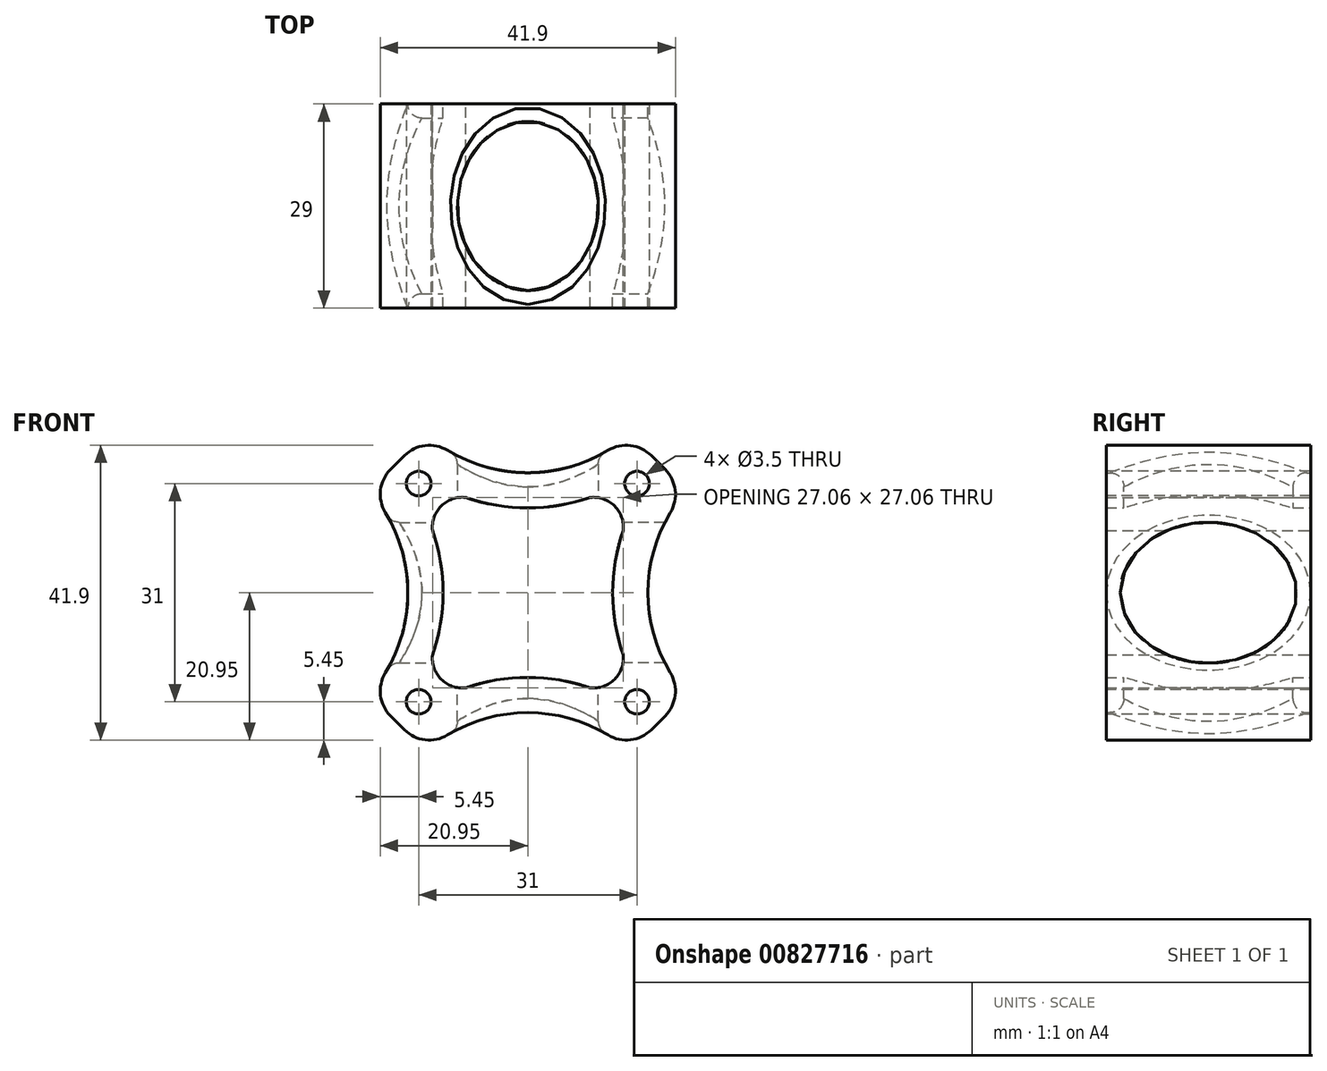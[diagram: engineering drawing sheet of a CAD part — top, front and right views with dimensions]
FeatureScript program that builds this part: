
annotation { "Feature Type Name" : "Feature", "Feature Type Description" : "" }
export const myFeature = defineFeature(function(context is Context, id is Id, definition is map)
    precondition{}
    {
        {
            var Q0;
            Q0=qCreatedBy(makeId("Front.planeOp"),FACE);
            var sketch = newSketch(context, id + "F0", { "sketchPlane" : qUnion([Q0])});
            skLineSegment(sketch, "E0.bottom", {"start": v(-15.5, 15.5) * mm, "end": v(15.5, 15.5) * mm, "construction": true});
            skLineSegment(sketch, "E0.top", {"start": v(-15.5, -15.5) * mm, "end": v(15.5, -15.5) * mm, "construction": true});
            skLineSegment(sketch, "E0.left", {"start": v(-15.5, 15.5) * mm, "end": v(-15.5, -15.5) * mm, "construction": true});
            skLineSegment(sketch, "E0.right", {"start": v(15.5, 15.5) * mm, "end": v(15.5, -15.5) * mm, "construction": true});
            skPoint(sketch, "E0.middle", {"position": v(0, 0) * mm});
            skCircle(sketch, "E1", {"center": v(-15.5, 15.5) * mm, "radius": 2.75 * mm, "construction": true});
            skCircle(sketch, "E2", {"center": v(15.5, 15.5) * mm, "radius": 2.75 * mm, "construction": true});
            skCircle(sketch, "E3", {"center": v(-15.5, -15.5) * mm, "radius": 2.75 * mm, "construction": true});
            skCircle(sketch, "E4", {"center": v(15.5, -15.5) * mm, "radius": 2.75 * mm, "construction": true});
            skCircle(sketch, "E5", {"center": v(0, 0) * mm, "radius": 6.6 * mm});
            skLineSegment(sketch, "E6.bottom", {"start": v(14.5, 22.5) * mm, "end": v(-14.5, 22.5) * mm});
            skLineSegment(sketch, "E6.top", {"start": v(14.5, -22.5) * mm, "end": v(-14.5, -22.5) * mm});
            skLineSegment(sketch, "E6.left", {"start": v(22.5, 14.5) * mm, "end": v(22.5, 0) * mm});
            skLineSegment(sketch, "E6.right", {"start": v(-22.5, 14.5) * mm, "end": v(-22.5, 0) * mm});
            skPoint(sketch, "E7.visualSharp", {"position": v(-22.5, 22.5) * mm});
            skPoint(sketch, "E8.visualSharp", {"position": v(22.5, 22.5) * mm});
            skPoint(sketch, "E9.visualSharp", {"position": v(22.5, -22.5) * mm});
            skPoint(sketch, "E10.visualSharp", {"position": v(-22.5, -22.5) * mm});
            skLineSegment(sketch, "E11", {"start": v(-22.5, 0) * mm, "end": v(-22.5, -14.5) * mm});
            skLineSegment(sketch, "E12", {"start": v(22.5, 0) * mm, "end": v(22.5, -14.5) * mm});
            skArc(sketch, "E13", {"start": v(-22.5, -14.5) * mm, "mid": v(-17.05, 0) * mm, "end": v(-22.5, 14.5) * mm});
            skArc(sketch, "E14", {"start": v(-14.5, 22.5) * mm, "mid": v(0, 17.05) * mm, "end": v(14.5, 22.5) * mm});
            skArc(sketch, "E15", {"start": v(22.5, 14.5) * mm, "mid": v(17.05, 0) * mm, "end": v(22.5, -14.5) * mm});
            skArc(sketch, "E16", {"start": v(14.5, -22.5) * mm, "mid": v(0, -17.05) * mm, "end": v(-14.5, -22.5) * mm});
            skArc(sketch, "E17", {"start": v(-8.83, 13.53) * mm, "mid": v(0, 12.05) * mm, "end": v(8.83, 13.53) * mm});
            skArc(sketch, "E18", {"start": v(-8.83, 13.53) * mm, "mid": v(-12.3, 12.3) * mm, "end": v(-13.53, 8.83) * mm});
            skArc(sketch, "E19.1.0", {"start": v(-13.53, -8.83) * mm, "mid": v(-12.3, -12.3) * mm, "end": v(-8.83, -13.53) * mm});
            skArc(sketch, "E19.2.0", {"start": v(8.83, -13.53) * mm, "mid": v(12.3, -12.3) * mm, "end": v(13.53, -8.83) * mm});
            skArc(sketch, "E19.3.0", {"start": v(13.53, 8.83) * mm, "mid": v(12.3, 12.3) * mm, "end": v(8.83, 13.53) * mm});
            skArc(sketch, "E20", {"start": v(13.53, 8.83) * mm, "mid": v(12.05, 0) * mm, "end": v(13.53, -8.83) * mm});
            skArc(sketch, "E21", {"start": v(8.83, -13.53) * mm, "mid": v(0, -12.05) * mm, "end": v(-8.83, -13.53) * mm});
            skArc(sketch, "E22", {"start": v(-13.53, -8.83) * mm, "mid": v(-12.05, 0) * mm, "end": v(-13.53, 8.83) * mm});
            skLineSegment(sketch, "E23", {"start": v(-22.5, 14.5) * mm, "end": v(-14.5, 22.5) * mm});
            skLineSegment(sketch, "E24", {"start": v(14.5, 22.5) * mm, "end": v(22.5, 14.5) * mm});
            skLineSegment(sketch, "E25", {"start": v(22.5, -14.5) * mm, "end": v(14.5, -22.5) * mm});
            skLineSegment(sketch, "E26", {"start": v(-14.5, -22.5) * mm, "end": v(-22.5, -14.5) * mm});
            skSolve(sketch);
        }
        {
            var Q0;
            Q0=makeQuery(id+"F0.imprint","IMPRINT",FACE,{"disambiguationData":[TD([[makeQuery(id+"F0.imprint","IMPRINT",EDGE,{"derivedFrom":sQuery(id+"F0.wireOp",EDGE,"E13")}),-1.0]])]});
            extrude(context, id + "F1", {"entities" : qUnion([Q0]), "flatOperationType" : FlatOperationType.REMOVE, "depth" : 29 * mm, "offsetDistance" : 25 * mm, "domain" : OperationDomain.MODEL});
        }
        {
            var Q0;
            Q0=sQuery(id+"F0.wireOp",VERTEX,"E0.bottom.end");
            var Q1;
            Q1=sQuery(id+"F0.wireOp",VERTEX,"E0.bottom.start");
            var Q2;
            Q2=sQuery(id+"F0.wireOp",VERTEX,"E0.top.start");
            var Q3;
            Q3=sQuery(id+"F0.wireOp",VERTEX,"E0.top.end");
            var Q4;
            Q4=makeQuery(id+"F1.opExtrude","SWEPT_BODY",BODY,{"disambiguationData":[OSD([sQuery(id+"F0.wireOp",EDGE,"E7.filletArc"),sQuery(id+"F0.wireOp",EDGE,"E8.filletArc"),sQuery(id+"F0.wireOp",EDGE,"E9.filletArc"),sQuery(id+"F0.wireOp",EDGE,"E10.filletArc"),sQuery(id+"F0.wireOp",EDGE,"E13"),sQuery(id+"F0.wireOp",EDGE,"E14"),sQuery(id+"F0.wireOp",EDGE,"E15"),sQuery(id+"F0.wireOp",EDGE,"E16"),sQuery(id+"F0.wireOp",EDGE,"E17"),sQuery(id+"F0.wireOp",EDGE,"E18"),sQuery(id+"F0.wireOp",EDGE,"E19.1.0"),sQuery(id+"F0.wireOp",EDGE,"E19.2.0"),sQuery(id+"F0.wireOp",EDGE,"E19.3.0"),sQuery(id+"F0.wireOp",EDGE,"E20"),sQuery(id+"F0.wireOp",EDGE,"E21"),sQuery(id+"F0.wireOp",EDGE,"E22")])]});
            hole(context, id + "F2", {"style" : HoleStyle.SIMPLE, "endStyle" : HoleEndStyle.THROUGH, "oppositeDirection" : true, "holeDiameter" : 3.5 * mm, "majorDiameter" : 5 * mm, "isTappedThrough" : true, "tappedDepth" : 12 * mm, "tapClearance" : 3, "locations" : qUnion([Q0, Q1, Q2, Q3]), "scope" : qUnion([Q4]), "startStyle" : HoleStartStyle.PART});
        }
        {
            var Q0;
            Q0=makeQuery(id+"F1.opExtrude","SWEPT_EDGE",EDGE,{"disambiguationData":[OSD([sQuery(id+"F0.wireOp",EDGE,"E6.right"),sQuery(id+"F0.wireOp",EDGE,"E13"),sQuery(id+"F0.wireOp",EDGE,"E23")])]});
            var Q1;
            Q1=makeQuery(id+"F1.opExtrude","SWEPT_EDGE",EDGE,{"disambiguationData":[OSD([sQuery(id+"F0.wireOp",EDGE,"E6.bottom"),sQuery(id+"F0.wireOp",EDGE,"E14"),sQuery(id+"F0.wireOp",EDGE,"E23")])]});
            var Q2;
            Q2=makeQuery(id+"F1.opExtrude","SWEPT_EDGE",EDGE,{"disambiguationData":[OSD([sQuery(id+"F0.wireOp",EDGE,"E6.bottom"),sQuery(id+"F0.wireOp",EDGE,"E14"),sQuery(id+"F0.wireOp",EDGE,"E24")])]});
            var Q3;
            Q3=makeQuery(id+"F1.opExtrude","SWEPT_EDGE",EDGE,{"disambiguationData":[OSD([sQuery(id+"F0.wireOp",EDGE,"E6.left"),sQuery(id+"F0.wireOp",EDGE,"E15"),sQuery(id+"F0.wireOp",EDGE,"E24")])]});
            var Q4;
            Q4=makeQuery(id+"F1.opExtrude","SWEPT_EDGE",EDGE,{"disambiguationData":[OSD([sQuery(id+"F0.wireOp",EDGE,"E12"),sQuery(id+"F0.wireOp",EDGE,"E15"),sQuery(id+"F0.wireOp",EDGE,"E25")])]});
            var Q5;
            Q5=makeQuery(id+"F1.opExtrude","SWEPT_EDGE",EDGE,{"disambiguationData":[OSD([sQuery(id+"F0.wireOp",EDGE,"E6.top"),sQuery(id+"F0.wireOp",EDGE,"E16"),sQuery(id+"F0.wireOp",EDGE,"E25")])]});
            var Q6;
            Q6=makeQuery(id+"F1.opExtrude","SWEPT_EDGE",EDGE,{"disambiguationData":[OSD([sQuery(id+"F0.wireOp",EDGE,"E6.top"),sQuery(id+"F0.wireOp",EDGE,"E16"),sQuery(id+"F0.wireOp",EDGE,"E26")])]});
            var Q7;
            Q7=makeQuery(id+"F1.opExtrude","SWEPT_EDGE",EDGE,{"disambiguationData":[OSD([sQuery(id+"F0.wireOp",EDGE,"E11"),sQuery(id+"F0.wireOp",EDGE,"E13"),sQuery(id+"F0.wireOp",EDGE,"E26")])]});
            fillet(context, id + "F3", {"entities" : qUnion([Q0, Q1, Q2, Q3, Q4, Q5, Q6, Q7]), "radius" : 5 * mm, "tangentPropagation" : true, "allowEdgeOverflow" : false});
        }
        {
            var Q0;
            Q0=qCreatedBy(makeId("Right.planeOp"),FACE);
            cPlane(context, id + "F4", {"entities" : qUnion([Q0]), "cplaneType" : CPlaneType.OFFSET, "offset" : 25 * mm, "width" : 150 * mm, "height" : 150 * mm});
        }
        {
            var Q0;
            Q0=qCreatedBy(id+"F4.planeOp",FACE);
            var sketch = newSketch(context, id + "F5", { "sketchPlane" : qUnion([Q0])});
            skArc(sketch, "E27", {"start": v(-2.5, 0) * mm, "mid": v(-14.5, 12) * mm, "end": v(-26.5, 0) * mm, "construction": true});
            skLineSegment(sketch, "E28", {"start": v(0, 0) * mm, "end": v(-29, 0) * mm});
            skCircle(sketch, "E29", {"center": v(-14.5, 0) * mm, "radius": 12 * mm, "construction": true});
            skEllipse(sketch, "E30", {"center": v(-14.5, 0) * mm, "majorRadius": 10 * mm, "minorRadius": 12.5 * mm, "majorAxis": v(0, 1)});
            skSolve(sketch);
        }
        {
            var Q0;
            Q0 = qSketchRegion(id + "F5", true);
            extrude(context, id + "F6", {"entities" : qUnion([Q0]), "operationType" : NewBodyOperationType.REMOVE, "oppositeDirection" : true, "depth" : 60 * mm, "offsetDistance" : 25 * mm});
        }
        {
            var Q0;
            Q0=qCreatedBy(makeId("Top.planeOp"),FACE);
            cPlane(context, id + "F7", {"entities" : qUnion([Q0]), "cplaneType" : CPlaneType.OFFSET, "offset" : 25 * mm, "width" : 150 * mm, "height" : 150 * mm});
        }
        {
            var Q0;
            Q0=qCreatedBy(id+"F7.planeOp",FACE);
            var sketch = newSketch(context, id + "F8", { "sketchPlane" : qUnion([Q0])});
            skLineSegment(sketch, "E31", {"start": v(0, 0) * mm, "end": v(0, -29) * mm});
            skCircle(sketch, "E32", {"center": v(0, -14.5) * mm, "radius": 12 * mm, "construction": true});
            skEllipse(sketch, "E33", {"center": v(0, -14.5) * mm, "majorRadius": 10 * mm, "minorRadius": 12 * mm, "majorAxis": v(-1, 0)});
            skSolve(sketch);
        }
        {
            var Q0;
            {var subQ0=sQuery(id+"F8.wireOp",EDGE,"E32");var subQ1=sQuery(id+"F8.wireOp",EDGE,"E31");var subQ2=makeQuery(id+"F8.imprint","INTERSECT",VERTEX,{"disambiguationData":[OD(0.0)],"derivedFrom":[subQ1,subQ0]});Q0=makeQuery(id+"F8.imprint","IMPRINT",FACE,{"disambiguationData":[TD([[makeQuery(id+"F8.imprint","IMPRINT",EDGE,{"disambiguationData":[TD([[subQ2,1.0]])],"derivedFrom":subQ1}),1.0]])]});}
            var Q1;
            {var subQ0=sQuery(id+"F8.wireOp",EDGE,"E32");var subQ1=sQuery(id+"F8.wireOp",EDGE,"E31");var subQ2=makeQuery(id+"F8.imprint","INTERSECT",VERTEX,{"disambiguationData":[OD(0.0)],"derivedFrom":[subQ1,subQ0]});Q1=makeQuery(id+"F8.imprint","IMPRINT",FACE,{"disambiguationData":[TD([[makeQuery(id+"F8.imprint","IMPRINT",EDGE,{"disambiguationData":[TD([[subQ2,1.0]])],"derivedFrom":subQ1}),-1.0]])]});}
            extrude(context, id + "F9", {"entities" : qUnion([Q0, Q1]), "operationType" : NewBodyOperationType.REMOVE, "oppositeDirection" : true, "depth" : 60 * mm, "offsetDistance" : 25 * mm});
        }
        {
            var Q0;
            Q0=makeQuery(id+"F9.boolean.opBoolean","INTERSECT",EDGE,{"disambiguationData":[OD(0.0)],"derivedFrom":[makeQuery(id+"F1.opExtrude","SWEPT_FACE",FACE,{"disambiguationData":[OSD([sQuery(id+"F0.wireOp",EDGE,"E14")])]}),makeQuery(id+"F9.opExtrude","SWEPT_FACE",FACE,{"disambiguationData":[OSD([sQuery(id+"F8.wireOp",EDGE,"E33")])]})]});
            var Q1;
            Q1=makeQuery(id+"F9.boolean.opBoolean","INTERSECT",EDGE,{"derivedFrom":[makeQuery(id+"F3.opFillet","BLEND_FACE",FACE,{"disambiguationData":[OSD([sQuery(id+"F0.wireOp",EDGE,"E6.bottom"),sQuery(id+"F0.wireOp",EDGE,"E14"),sQuery(id+"F0.wireOp",EDGE,"E23")])]}),makeQuery(id+"F9.opExtrude","SWEPT_FACE",FACE,{"disambiguationData":[OSD([sQuery(id+"F8.wireOp",EDGE,"E33")])]})]});
            var Q2;
            Q2=makeQuery(id+"F9.boolean.opBoolean","INTERSECT",EDGE,{"disambiguationData":[OD(1.0)],"derivedFrom":[makeQuery(id+"F1.opExtrude","SWEPT_FACE",FACE,{"disambiguationData":[OSD([sQuery(id+"F0.wireOp",EDGE,"E14")])]}),makeQuery(id+"F9.opExtrude","SWEPT_FACE",FACE,{"disambiguationData":[OSD([sQuery(id+"F8.wireOp",EDGE,"E33")])]})]});
            var Q3;
            Q3=makeQuery(id+"F9.boolean.opBoolean","INTERSECT",EDGE,{"derivedFrom":[makeQuery(id+"F3.opFillet","BLEND_FACE",FACE,{"disambiguationData":[OSD([sQuery(id+"F0.wireOp",EDGE,"E6.bottom"),sQuery(id+"F0.wireOp",EDGE,"E14"),sQuery(id+"F0.wireOp",EDGE,"E24")])]}),makeQuery(id+"F9.opExtrude","SWEPT_FACE",FACE,{"disambiguationData":[OSD([sQuery(id+"F8.wireOp",EDGE,"E33")])]})]});
            var Q4;
            Q4=makeQuery(id+"F6.boolean.opBoolean","INTERSECT",EDGE,{"disambiguationData":[OD(0.0)],"derivedFrom":[makeQuery(id+"F1.opExtrude","SWEPT_FACE",FACE,{"disambiguationData":[OSD([sQuery(id+"F0.wireOp",EDGE,"E13")])]}),makeQuery(id+"F6.opExtrude","SWEPT_FACE",FACE,{"disambiguationData":[OSD([sQuery(id+"F5.wireOp",EDGE,"E30")])]})]});
            var Q5;
            Q5=makeQuery(id+"F6.boolean.opBoolean","INTERSECT",EDGE,{"derivedFrom":[makeQuery(id+"F3.opFillet","BLEND_FACE",FACE,{"disambiguationData":[OSD([sQuery(id+"F0.wireOp",EDGE,"E6.left"),sQuery(id+"F0.wireOp",EDGE,"E15"),sQuery(id+"F0.wireOp",EDGE,"E24")])]}),makeQuery(id+"F6.opExtrude","SWEPT_FACE",FACE,{"disambiguationData":[OSD([sQuery(id+"F5.wireOp",EDGE,"E30")])]})]});
            var Q6;
            Q6=makeQuery(id+"F9.boolean.opBoolean","INTERSECT",EDGE,{"disambiguationData":[OD(0.0)],"derivedFrom":[makeQuery(id+"F1.opExtrude","SWEPT_FACE",FACE,{"disambiguationData":[OSD([sQuery(id+"F0.wireOp",EDGE,"E16")])]}),makeQuery(id+"F9.opExtrude","SWEPT_FACE",FACE,{"disambiguationData":[OSD([sQuery(id+"F8.wireOp",EDGE,"E33")])]})]});
            fillet(context, id + "F10", {"entities" : qUnion([Q0, Q1, Q2, Q3, Q4, Q5, Q6]), "radius" : 2 * mm, "tangentPropagation" : true, "allowEdgeOverflow" : false});
        }
    });
